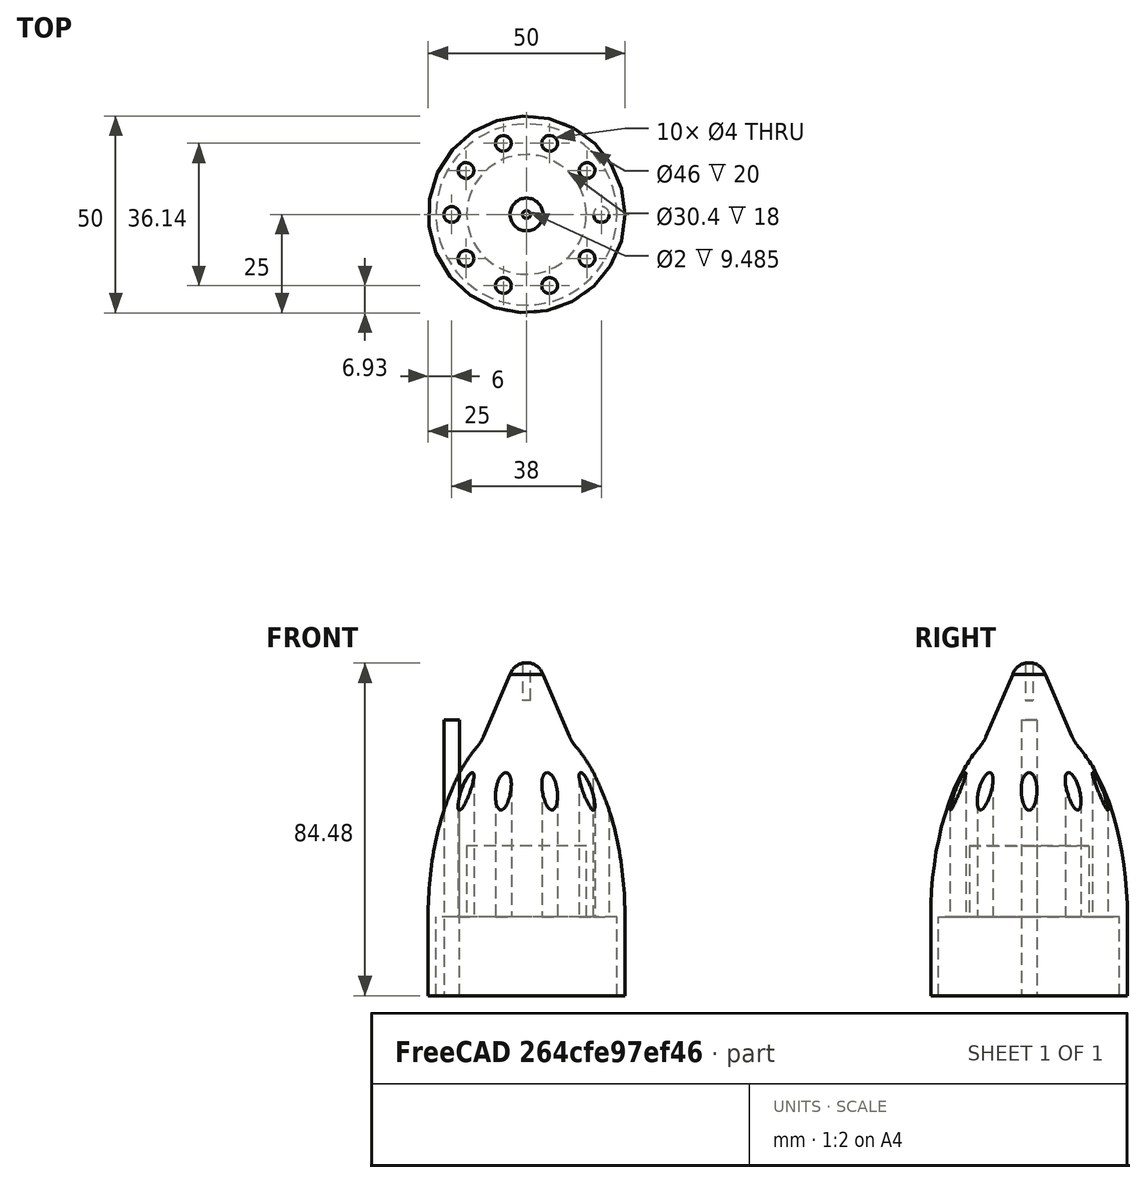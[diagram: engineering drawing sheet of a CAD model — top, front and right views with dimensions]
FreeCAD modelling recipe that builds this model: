
FCSTD DOCUMENT  (FreeCAD 1.0R39109 (Git))
Label: Ojiva
License: All rights reserved
LicenseURL: http://en.wikipedia.org/wiki/All_rights_reserved
objects: Part::Cut×4, Part::MultiFuse×3, Part::Cylinder×3, Part::FeaturePython×2, Part::Ellipsoid×1, Part::Cone×1, Part::Sphere×1, Part::Box×1, Part::Fillet×1
note: 16 computed .brp shape members not serialized (recipe doc carries the construction recipe); baked Part::Feature solids carry a one-line shape summary decoded from their .brp

FEATURE [Part::Ellipsoid] Ellipsoid  label="Elipsoide"
  Angle1 = -90
  Angle2 = 90
  Angle3 = 360
  AttacherType = Attacher::AttachEngine3D
  Radius1 = 50
  Radius2 = 25
  Radius3 = 25
FEATURE [Part::Cone] Cone  label="Cono"
  Angle = 360
  AttacherType = Attacher::AttachEngine3D
  Height = 28
  Placement = pos=(0,0,63) rot=(0,1,0;3.14159rad)
  Radius1 = 4
  Radius2 = 16
FEATURE [Part::Sphere] Sphere  label="Esfera"
  Angle1 = -90
  Angle2 = 90
  Angle3 = 360
  AttacherType = Attacher::AttachEngine3D
  Placement = pos=(0,0,61.2) rot=(0,0,1;0rad)
  Radius = 4.4
FEATURE [Part::MultiFuse] Fusion
  Placement = pos=(0,0,-1) rot=(0,0,1;0rad)
  Shapes = -> [Cone,Sphere]
FEATURE [Part::Box] Box  label="Cubo"
  AttacherType = Attacher::AttachEngine3D
  Height = 80
  Length = 80
  Placement = pos=(-35,-50,-80) rot=(0,0,1;0rad)
  Width = 80
FEATURE [Part::Cylinder] Cylinder  label="Cilindro"
  Angle = 360
  AttacherType = Attacher::AttachEngine3D
  FirstAngle = 0
  Height = 18
  Radius = 15.2
  SecondAngle = 0
FEATURE [Part::MultiFuse] Fusion001
  Shapes = -> [Ellipsoid,Fusion]
FEATURE [Part::Fillet] Fillet
  Base = -> Fusion001
  EdgeLinks = -> Fusion001 [Edge2]
  Edges = 1 edges r=10: [Edge2]
FEATURE [Part::Cut] Cut
  Base = -> Fillet
  Tool = -> Box
FEATURE [Part::Cut] Cut001
  Base = -> Cut
  Tool = -> Cylinder
FEATURE [Part::FeaturePython] Tube  # WARN: FeaturePython — macro-defined, semantics opaque (R4)
  AttacherType = Attacher::AttachEngine3D
  Height = 20
  InnerRadius = 23
  OuterRadius = 25
  Placement = pos=(0,0,-20) rot=(0,0,1;0rad)
FEATURE [Part::MultiFuse] Fusion002
  Placement = pos=(0,0,20) rot=(0,0,1;0rad)
  Shapes = -> [Cut001,Tube]
FEATURE [Part::Cylinder] Cylinder001  label="Cilindro001"
  Angle = 360
  AttacherType = Attacher::AttachEngine3D
  FirstAngle = 0
  Height = 10
  Placement = pos=(0,0,75) rot=(0,0,1;0rad)
  Radius = 1
  SecondAngle = 0
FEATURE [Part::Cut] Cut002
  Base = -> Fusion002
  Tool = -> Cylinder001
FEATURE [Part::Cylinder] Cylinder002  label="Cilindro002"
  Angle = 360
  AttacherType = Attacher::AttachEngine3D
  FirstAngle = 0
  Height = 70
  Placement = pos=(-19,0,0) rot=(0,0,1;0rad)
  Radius = 2
  SecondAngle = 0
FEATURE [Part::FeaturePython] Array  # Draft array (typed FeaturePython)
  AlwaysSyncPlacement = false
  Angle = 360
  ArrayType = 1
  Axis = (0,0,1)
  Base = -> Cylinder002
  Center = (0,0,0)
  Count = 10
  ExpandArray = false
  Fuse = false
  IntervalAxis = (0,0,0)
  IntervalX = (50,0,0)
  IntervalY = (0,50,0)
  IntervalZ = (0,0,50)
  NumberCircles = 3
  NumberPolar = 10
  NumberX = 2
  NumberY = 2
  NumberZ = 1
  PlacementList = 10 placements: [(-19,0,0),(-15.3713,-11.1679,0),(-5.87132,-18.0701,0),(5.87132,-18.0701,0),(15.3713,-11.1679,0),(19,-2.32683e-15,0),(15.3713,11.1679,0),(5.87132,18.0701,0),(-5.87132,18.0701,0),(-15.3713,11.1679,0)]
  RadialDistance = 50
  ScaleList = (10) [(1,1,1),(1,1,1),(1,1,1),(1,1,1),(1,1,1),(1,1,1),(1,1,1),(1,1,1),(1,1,1),(1,1,1)]
  Symmetry = 1
  TangentialDistance = 25
FEATURE [Part::Cut] Cut003
  Base = -> Cut002
  Tool = -> Array
